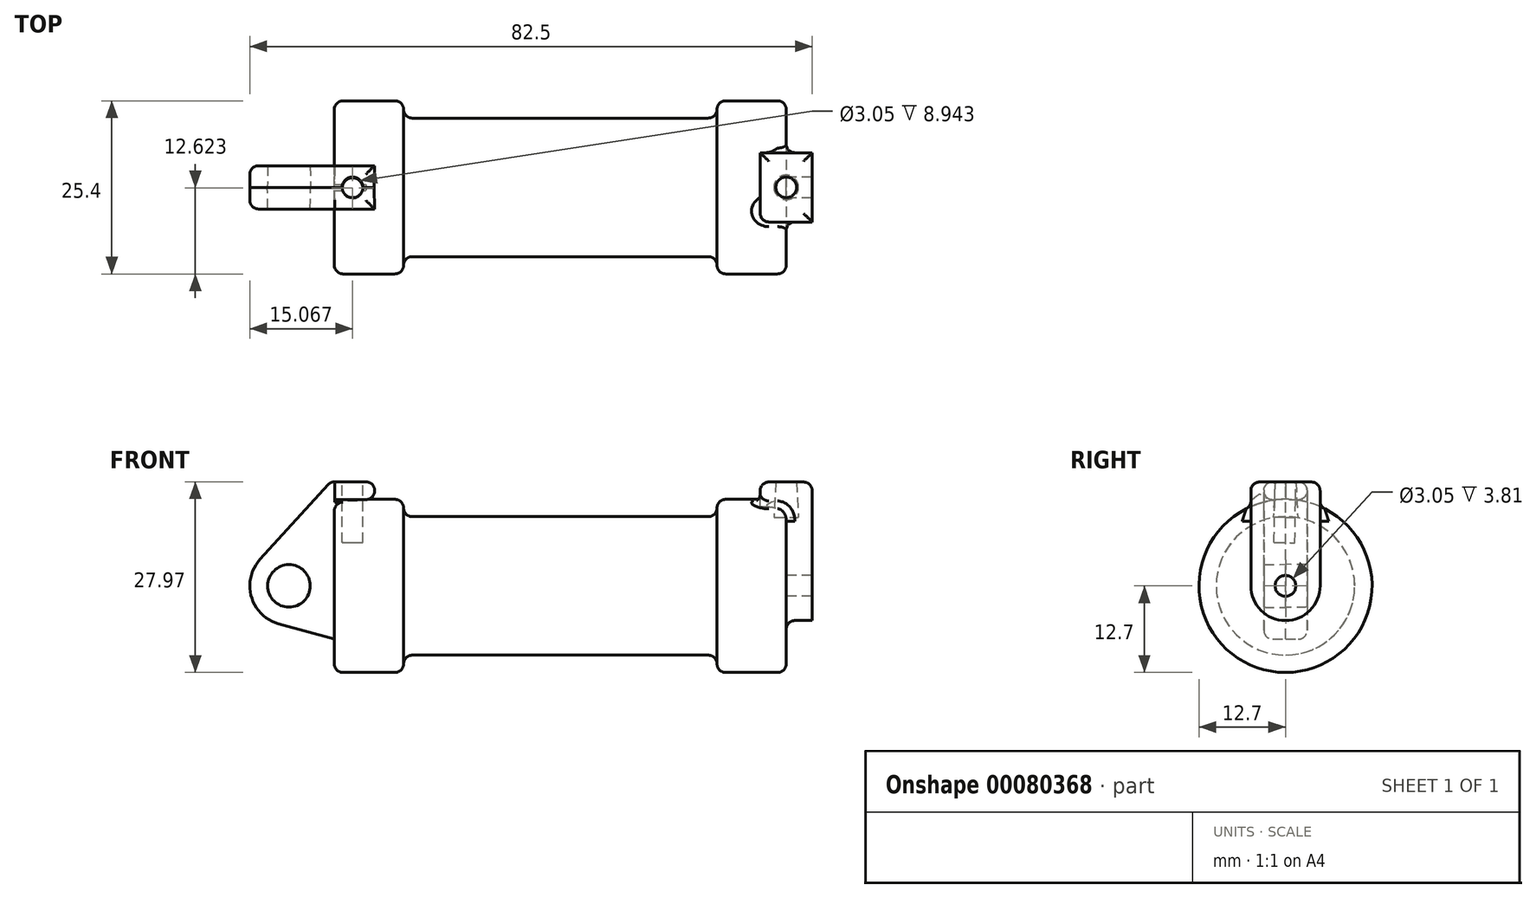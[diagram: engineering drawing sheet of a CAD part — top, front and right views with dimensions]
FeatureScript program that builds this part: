
annotation { "Feature Type Name" : "Feature", "Feature Type Description" : "" }
export const myFeature = defineFeature(function(context is Context, id is Id, definition is map)
    precondition{}
    {
        {
            var Q0;
            Q0=qCreatedBy(makeId("Front.planeOp"),FACE);
            var sketch = newSketch(context, id + "F0", { "sketchPlane" : qUnion([Q0])});
            skLineSegment(sketch, "E0", {"start": v(0, 0) * mm, "end": v(0, 12.7) * mm});
            skLineSegment(sketch, "E1", {"start": v(0, 12.7) * mm, "end": v(10.16, 12.7) * mm});
            skLineSegment(sketch, "E2", {"start": v(10.16, 12.7) * mm, "end": v(10.16, 10.16) * mm});
            skLineSegment(sketch, "E3", {"start": v(10.16, 10.16) * mm, "end": v(56.13, 10.16) * mm});
            skLineSegment(sketch, "E4", {"start": v(56.13, 10.16) * mm, "end": v(56.13, 12.7) * mm});
            skLineSegment(sketch, "E5", {"start": v(56.13, 12.7) * mm, "end": v(66.3, 12.7) * mm});
            skLineSegment(sketch, "E6", {"start": v(66.3, 12.7) * mm, "end": v(66.3, 0) * mm});
            skLineSegment(sketch, "E7", {"start": v(66.3, 0) * mm, "end": v(0, 0) * mm});
            skLineSegment(sketch, "E8", {"start": v(5.84, 15.24) * mm, "end": v(-0.5, 15.24) * mm});
            skLineSegment(sketch, "E9", {"start": v(-0.5, 15.24) * mm, "end": v(-10.88, 3.85) * mm});
            skLineSegment(sketch, "E10", {"start": v(0, 0) * mm, "end": v(-6.65, 0) * mm});
            skCircle(sketch, "E11", {"center": v(-6.65, 0) * mm, "radius": 5.72 * mm});
            skCircle(sketch, "E12", {"center": v(-6.65, 0) * mm, "radius": 3.18 * mm});
            skLineSegment(sketch, "E13", {"start": v(5.84, 15.24) * mm, "end": v(5.84, -9.4) * mm});
            skLineSegment(sketch, "E14", {"start": v(5.84, -9.4) * mm, "end": v(-8.18, -5.5) * mm});
            skSolve(sketch);
        }
        {
            var Q0;
            {var subQ0=sQuery(id+"F0.wireOp",EDGE,"E2");Q0=makeQuery(id+"F0.imprint","IMPRINT",FACE,{"disambiguationData":[TD([[makeQuery(id+"F0.imprint","IMPRINT",EDGE,{"derivedFrom":subQ0}),-1.0]])]});}
            var Q1;
            {var subQ0=sQuery(id+"F0.wireOp",EDGE,"E0");Q1=makeQuery(id+"F0.imprint","IMPRINT",FACE,{"disambiguationData":[TD([[makeQuery(id+"F0.imprint","IMPRINT",EDGE,{"derivedFrom":subQ0}),-1.0]])]});}
            var Q2;
            Q2=sQuery(id+"F0.wireOp",EDGE,"E7");
            revolve(context, id + "F1", {"entities" : qUnion([Q0, Q1]), "axis" : qUnion([Q2]), "revolveType" : RevolveType.FULL});
        }
        {
            var Q0;
            {var subQ3=sQuery(id+"F0.wireOp",EDGE,"E0");Q0=makeQuery(id+"F0.imprint","IMPRINT",FACE,{"disambiguationData":[TD([[makeQuery(id+"F0.imprint","IMPRINT",EDGE,{"derivedFrom":subQ3}),1.0]])]});}
            var Q1;
            {var subQ0=sQuery(id+"F0.wireOp",EDGE,"E14");Q1=makeQuery(id+"F0.imprint","IMPRINT",FACE,{"disambiguationData":[TD([[makeQuery(id+"F0.imprint","IMPRINT",EDGE,{"derivedFrom":subQ0}),-1.0]])]});}
            var Q2;
            {var subQ4=sQuery(id+"F0.wireOp",EDGE,"E12");Q2=makeQuery(id+"F0.imprint","IMPRINT",FACE,{"disambiguationData":[TD([[makeQuery(id+"F0.imprint","IMPRINT",EDGE,{"derivedFrom":subQ4}),-1.0]])]});}
            extrude(context, id + "F2", {"entities" : qUnion([Q0, Q1, Q2]), "operationType" : NewBodyOperationType.ADD, "endBound" : BoundingType.SYMMETRIC, "depth" : 6.35 * mm, "hasDraft" : true, "draftAngle" : 1 * degree});
        }
        {
            var Q0;
            Q0=makeQuery(id+"F1.opRevolve","SWEPT_FACE",FACE,{"disambiguationData":[OSD([sQuery(id+"F0.wireOp",EDGE,"E6")])]});
            var sketch = newSketch(context, id + "F3", { "sketchPlane" : qUnion([Q0])});
            skCircle(sketch, "E15", {"center": v(0, 0) * mm, "radius": 1.52 * mm});
            skCircle(sketch, "E16", {"center": v(0, 0) * mm, "radius": 5.08 * mm});
            skLineSegment(sketch, "E17", {"start": v(5.08, 0) * mm, "end": v(5.08, 15.24) * mm});
            skLineSegment(sketch, "E18", {"start": v(-5.08, 0) * mm, "end": v(-5.08, 15.24) * mm});
            skLineSegment(sketch, "E19", {"start": v(-5.08, 15.24) * mm, "end": v(5.08, 15.24) * mm});
            skSolve(sketch);
        }
        {
            var Q0;
            Q0=makeQuery(id+"F3.imprint","IMPRINT",FACE,{"disambiguationData":[TD([[makeQuery(id+"F3.imprint","IMPRINT",EDGE,{"derivedFrom":sQuery(id+"F3.wireOp",EDGE,"E15")}),-1.0]])]});
            var Q1;
            {var subQ0=sQuery(id+"F3.wireOp",EDGE,"E17");var subQ1=sQuery(id+"F3.wireOp",EDGE,"E16");var subQ2=makeQuery(id+"F3.imprint","INTERSECT",VERTEX,{"derivedFrom":[subQ1,subQ0]});Q1=makeQuery(id+"F3.imprint","IMPRINT",FACE,{"disambiguationData":[TD([[makeQuery(id+"F3.imprint","IMPRINT",EDGE,{"disambiguationData":[TD([[subQ2,-1.0]])],"derivedFrom":subQ1}),-1.0]])]});}
            var Q2;
            {var subQ0=sQuery(id+"F3.wireOp",EDGE,"E19");Q2=makeQuery(id+"F3.imprint","IMPRINT",FACE,{"disambiguationData":[TD([[makeQuery(id+"F3.imprint","IMPRINT",EDGE,{"derivedFrom":subQ0}),-1.0]])]});}
            extrude(context, id + "F4", {"entities" : qUnion([Q0, Q1, Q2]), "operationType" : NewBodyOperationType.ADD, "endBound" : BoundingType.SYMMETRIC, "depth" : 7.62 * mm});
        }
        {
            var Q0;
            Q0=makeQuery(id+"F4.opExtrude","SWEPT_FACE",FACE,{"disambiguationData":[OSD([sQuery(id+"F3.wireOp",EDGE,"E19")])]});
            var sketch = newSketch(context, id + "F5", { "sketchPlane" : qUnion([Q0])});
            skCircle(sketch, "E20", {"center": v(66.3, 0) * mm, "radius": 1.52 * mm});
            skPoint(sketch, "E20.centerSnap0", {"position": v(62.48, 0) * mm});
            skPoint(sketch, "E20.centerSnap1", {"position": v(66.3, -5.08) * mm});
            skSolve(sketch);
        }
        {
            var Q0;
            Q0 = qSketchRegion(id + "F5", true);
            extrude(context, id + "F6", {"entities" : qUnion([Q0]), "operationType" : NewBodyOperationType.REMOVE, "endBound" : BoundingType.SYMMETRIC, "oppositeDirection" : true, "depth" : 10.4 * mm, "hasDraft" : true, "draftAngle" : 3 * degree});
        }
        {
            var Q0;
            Q0=makeQuery(id+"F2.split0.splitOp","SPLIT",FACE,{"derivedFrom":makeQuery(id+"F2.opExtrude","SWEPT_FACE",FACE,{"disambiguationData":[OSD([sQuery(id+"F0.wireOp",EDGE,"E8")])]})});
            var sketch = newSketch(context, id + "F7", { "sketchPlane" : qUnion([Q0])});
            skCircle(sketch, "E21", {"center": v(2.67, -0.27) * mm, "radius": 1.52 * mm});
            skSolve(sketch);
        }
        {
            var Q0;
            Q0 = qSketchRegion(id + "F7", true);
            extrude(context, id + "F8", {"entities" : qUnion([Q0]), "operationType" : NewBodyOperationType.REMOVE, "endBound" : BoundingType.SYMMETRIC, "oppositeDirection" : true, "depth" : 17.78 * mm});
        }
        {
            var Q0;
            Q0=makeQuery(id+"F1.opRevolve","SWEPT_FACE",FACE,{"disambiguationData":[OSD([sQuery(id+"F0.wireOp",EDGE,"E4")])]});
            var Q1;
            Q1=makeQuery(id+"F1.opRevolve","SWEPT_FACE",FACE,{"disambiguationData":[OSD([sQuery(id+"F0.wireOp",EDGE,"E2")])]});
            var Q2;
            Q2=makeQuery(id+"F1.opRevolve","SWEPT_EDGE",EDGE,{"disambiguationData":[OSD([sQuery(id+"F0.wireOp",EDGE,"E0"),sQuery(id+"F0.wireOp",EDGE,"E1")])]});
            var Q3;
            Q3=makeQuery(id+"F1.opRevolve","SWEPT_EDGE",EDGE,{"disambiguationData":[OSD([sQuery(id+"F0.wireOp",EDGE,"E5"),sQuery(id+"F0.wireOp",EDGE,"E6")])]});
            var Q4;
            Q4=makeQuery(id+"F2.opExtrude","CAP_EDGE",EDGE,{"disambiguationData":[OSD([sQuery(id+"F0.wireOp",EDGE,"E8")])],"isStart":false});
            var Q5;
            Q5=makeQuery(id+"F2.split0.splitOp","SPLIT",EDGE,{"derivedFrom":makeQuery(id+"F2.opExtrude","SWEPT_EDGE",EDGE,{"disambiguationData":[OSD([sQuery(id+"F0.wireOp",EDGE,"E8"),sQuery(id+"F0.wireOp",EDGE,"E13")])]})});
            var Q6;
            Q6=makeQuery(id+"F2.split0.splitOp","SPLIT",EDGE,{"derivedFrom":makeQuery(id+"F2.opExtrude","SWEPT_EDGE",EDGE,{"disambiguationData":[OSD([sQuery(id+"F0.wireOp",EDGE,"E8"),sQuery(id+"F0.wireOp",EDGE,"E13")])]}),"isFromBackBody":true});
            var Q7;
            Q7=makeQuery(id+"F2.opExtrude","CAP_EDGE",EDGE,{"disambiguationData":[OSD([sQuery(id+"F0.wireOp",EDGE,"E8")])],"isStart":true});
            var Q8;
            Q8=makeQuery(id+"F2.split0.splitOp","SPLIT",EDGE,{"derivedFrom":makeQuery(id+"F2.opExtrude","SWEPT_EDGE",EDGE,{"disambiguationData":[OSD([sQuery(id+"F0.wireOp",EDGE,"E8"),sQuery(id+"F0.wireOp",EDGE,"E9")])]})});
            var Q9;
            Q9=makeQuery(id+"F2.split0.splitOp","SPLIT",EDGE,{"derivedFrom":makeQuery(id+"F2.opExtrude","SWEPT_EDGE",EDGE,{"disambiguationData":[OSD([sQuery(id+"F0.wireOp",EDGE,"E8"),sQuery(id+"F0.wireOp",EDGE,"E9")])]}),"isFromBackBody":true});
            var Q10;
            Q10=makeQuery(id+"F4.opExtrude","SWEPT_EDGE",EDGE,{"disambiguationData":[OSD([sQuery(id+"F3.wireOp",EDGE,"E18"),sQuery(id+"F3.wireOp",EDGE,"E19")])]});
            var Q11;
            Q11=makeQuery(id+"F4.opExtrude","CAP_EDGE",EDGE,{"disambiguationData":[OSD([sQuery(id+"F3.wireOp",EDGE,"E18")])],"isStart":true});
            var Q12;
            Q12=makeQuery(id+"F4.boolean.opBoolean","INTERSECT",EDGE,{"derivedFrom":[makeQuery(id+"F1.opRevolve","SWEPT_FACE",FACE,{"disambiguationData":[OSD([sQuery(id+"F0.wireOp",EDGE,"E5")])]}),makeQuery(id+"F4.opExtrude","SWEPT_FACE",FACE,{"disambiguationData":[OSD([sQuery(id+"F3.wireOp",EDGE,"E18")])]})]});
            var Q13;
            Q13=makeQuery(id+"F4.boolean.opBoolean","INTERSECT",EDGE,{"derivedFrom":[makeQuery(id+"F1.opRevolve","SWEPT_FACE",FACE,{"disambiguationData":[OSD([sQuery(id+"F0.wireOp",EDGE,"E6")])]}),makeQuery(id+"F4.opExtrude","SWEPT_FACE",FACE,{"disambiguationData":[OSD([sQuery(id+"F3.wireOp",EDGE,"E18")])]})]});
            var Q14;
            Q14=makeQuery(id+"F2.opExtrude","CAP_EDGE",EDGE,{"disambiguationData":[OSD([sQuery(id+"F0.wireOp",EDGE,"E9")])],"isStart":true});
            var Q15;
            Q15=makeQuery(id+"F2.opExtrude","CAP_EDGE",EDGE,{"disambiguationData":[OSD([sQuery(id+"F0.wireOp",EDGE,"E9")])],"isStart":false});
            var Q16;
            Q16=makeQuery(id+"F4.opExtrude","CAP_EDGE",EDGE,{"disambiguationData":[OSD([sQuery(id+"F3.wireOp",EDGE,"E19")])],"isStart":true});
            var Q17;
            Q17=makeQuery(id+"F4.opExtrude","SWEPT_EDGE",EDGE,{"disambiguationData":[OSD([sQuery(id+"F3.wireOp",EDGE,"E17"),sQuery(id+"F3.wireOp",EDGE,"E19")])]});
            var Q18;
            Q18=makeQuery(id+"F4.opExtrude","CAP_EDGE",EDGE,{"disambiguationData":[OSD([sQuery(id+"F3.wireOp",EDGE,"E19")])],"isStart":false});
            var Q19;
            Q19=makeQuery(id+"F2.opExtrude","CAP_EDGE",EDGE,{"disambiguationData":[OSD([sQuery(id+"F0.wireOp",EDGE,"E1")])],"isStart":false});
            var Q20;
            Q20=makeQuery(id+"F2.boolean.opBoolean","SPLIT",EDGE,{"derivedFrom":makeQuery(id+"F2.split0.splitOp","SPLIT",EDGE,{"derivedFrom":makeQuery(id+"F2.opExtrude","SWEPT_EDGE",EDGE,{"disambiguationData":[OSD([sQuery(id+"F0.wireOp",EDGE,"E1"),sQuery(id+"F0.wireOp",EDGE,"E13")])]})})});
            var Q21;
            Q21=makeQuery(id+"F2.boolean.opBoolean","SPLIT",EDGE,{"derivedFrom":makeQuery(id+"F2.split0.splitOp","SPLIT",EDGE,{"derivedFrom":makeQuery(id+"F2.opExtrude","SWEPT_EDGE",EDGE,{"disambiguationData":[OSD([sQuery(id+"F0.wireOp",EDGE,"E1"),sQuery(id+"F0.wireOp",EDGE,"E13")])]}),"isFromBackBody":true})});
            var Q22;
            Q22=makeQuery(id+"F2.opExtrude","CAP_EDGE",EDGE,{"disambiguationData":[OSD([sQuery(id+"F0.wireOp",EDGE,"E1")])],"isStart":true});
            fillet(context, id + "F9", {"entities" : qUnion([Q0, Q1, Q2, Q3, Q4, Q5, Q6, Q7, Q8, Q9, Q10, Q11, Q12, Q13, Q14, Q15, Q16, Q17, Q18, Q19, Q20, Q21, Q22]), "radius" : 1.27 * mm, "tangentPropagation" : true, "allowEdgeOverflow" : false});
        }
    });
